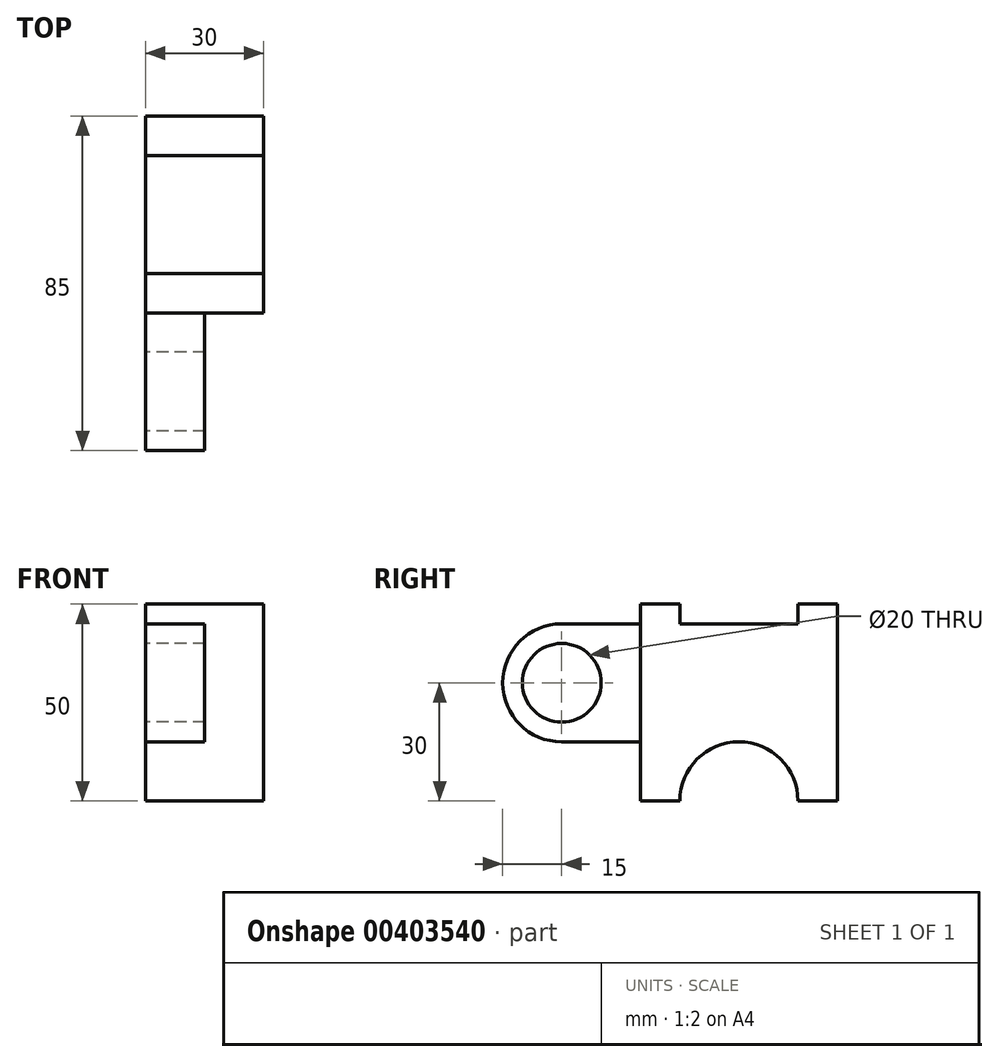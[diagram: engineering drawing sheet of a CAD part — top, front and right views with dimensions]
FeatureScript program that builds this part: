
annotation { "Feature Type Name" : "Feature", "Feature Type Description" : "" }
export const myFeature = defineFeature(function(context is Context, id is Id, definition is map)
    precondition{}
    {
        {
            var Q0;
            Q0=qCreatedBy(makeId("Right.planeOp"),FACE);
            var sketch = newSketch(context, id + "F0", { "sketchPlane" : qUnion([Q0])});
            skLineSegment(sketch, "E0.bottom", {"start": v(-25, 25) * mm, "end": v(25, 25) * mm});
            skLineSegment(sketch, "E0.top", {"start": v(-25, -25) * mm, "end": v(25, -25) * mm});
            skLineSegment(sketch, "E0.left", {"start": v(-25, 25) * mm, "end": v(-25, -25) * mm});
            skLineSegment(sketch, "E0.right", {"start": v(25, 25) * mm, "end": v(25, -25) * mm});
            skPoint(sketch, "E0.middle", {"position": v(0, 0) * mm});
            skSolve(sketch);
        }
        {
            var Q0;
            Q0 = qSketchRegion(id + "F0", true);
            extrude(context, id + "F1", {"entities" : qUnion([Q0]), "oppositeDirection" : true, "depth" : 30 * mm});
        }
        {
            var Q0;
            Q0=makeQuery(id+"F1.opExtrude","CAP_FACE",FACE,{"disambiguationData":[OSD([sQuery(id+"F0.wireOp",EDGE,"E0.bottom"),sQuery(id+"F0.wireOp",EDGE,"E0.top"),sQuery(id+"F0.wireOp",EDGE,"E0.left"),sQuery(id+"F0.wireOp",EDGE,"E0.right")])],"isStart":true});
            var sketch = newSketch(context, id + "F2", { "sketchPlane" : qUnion([Q0])});
            skLineSegment(sketch, "E1.bottom", {"start": v(-15, 25) * mm, "end": v(15, 25) * mm});
            skLineSegment(sketch, "E1.top", {"start": v(-15, 20) * mm, "end": v(15, 20) * mm});
            skLineSegment(sketch, "E1.left", {"start": v(-15, 25) * mm, "end": v(-15, 20) * mm});
            skLineSegment(sketch, "E1.right", {"start": v(15, 25) * mm, "end": v(15, 20) * mm});
            skCircle(sketch, "E2", {"center": v(0, -25) * mm, "radius": 15 * mm});
            skSolve(sketch);
        }
        {
            var Q0;
            Q0 = qSketchRegion(id + "F2", true);
            extrude(context, id + "F3", {"entities" : qUnion([Q0]), "operationType" : NewBodyOperationType.REMOVE, "endBound" : BoundingType.THROUGH_ALL, "oppositeDirection" : true, "depth" : 25 * mm});
        }
        {
            var Q0;
            Q0=makeQuery(id+"F1.opExtrude","CAP_FACE",FACE,{"disambiguationData":[OSD([sQuery(id+"F0.wireOp",EDGE,"E0.bottom"),sQuery(id+"F0.wireOp",EDGE,"E0.top"),sQuery(id+"F0.wireOp",EDGE,"E0.left"),sQuery(id+"F0.wireOp",EDGE,"E0.right")])],"isStart":false});
            var sketch = newSketch(context, id + "F4", { "sketchPlane" : qUnion([Q0])});
            skLineSegment(sketch, "E3.bottom", {"start": v(25, 20) * mm, "end": v(45, 20) * mm});
            skLineSegment(sketch, "E3.top", {"start": v(25, -10) * mm, "end": v(45, -10) * mm});
            skLineSegment(sketch, "E3.left", {"start": v(25, 20) * mm, "end": v(25, -10) * mm});
            skLineSegment(sketch, "E3.right", {"start": v(60, 5) * mm, "end": v(60, 5) * mm});
            skPoint(sketch, "E4.visualSharp", {"position": v(60, 20) * mm});
            skArc(sketch, "E4.filletArc", {"start": v(60, 5) * mm, "mid": v(55.6, 15.6) * mm, "end": v(45, 20) * mm});
            skPoint(sketch, "E5.visualSharp", {"position": v(60, -10) * mm});
            skArc(sketch, "E5.filletArc", {"start": v(45, -10) * mm, "mid": v(55.6, -5.6) * mm, "end": v(60, 5) * mm});
            skCircle(sketch, "E6", {"center": v(45, 5) * mm, "radius": 10 * mm});
            skSolve(sketch);
        }
        {
            var Q0;
            Q0 = qSketchRegion(id + "F4", true);
            extrude(context, id + "F5", {"entities" : qUnion([Q0]), "operationType" : NewBodyOperationType.ADD, "oppositeDirection" : true, "depth" : 15 * mm});
        }
    });
